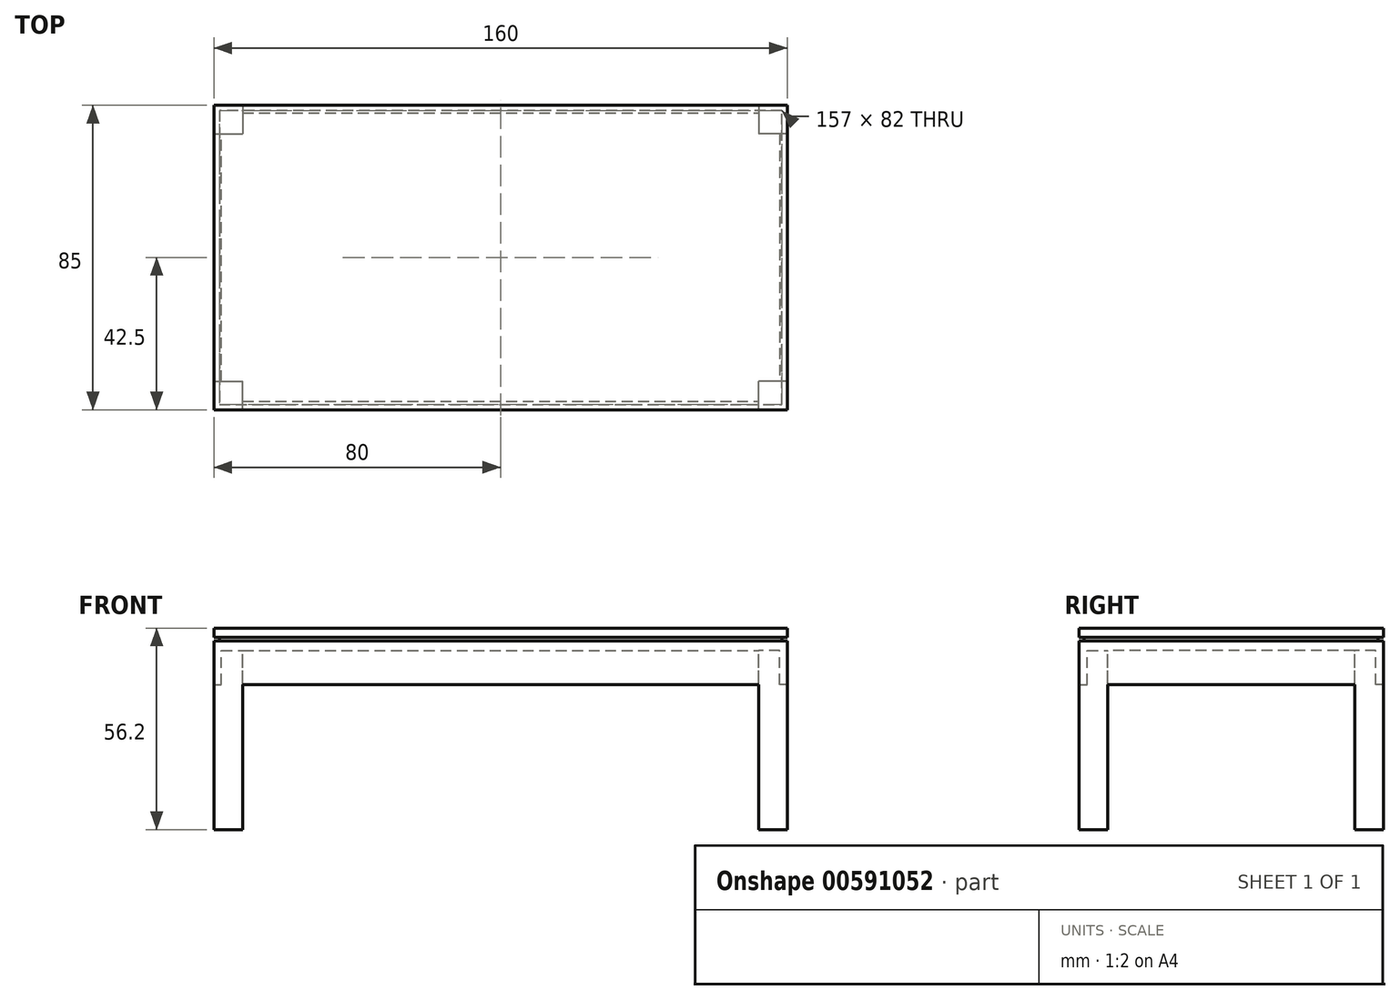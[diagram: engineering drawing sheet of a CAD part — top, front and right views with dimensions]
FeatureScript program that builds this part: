
annotation { "Feature Type Name" : "Feature", "Feature Type Description" : "" }
export const myFeature = defineFeature(function(context is Context, id is Id, definition is map)
    precondition{}
    {
        {
            var Q0;
            Q0=qCreatedBy(makeId("Top.planeOp"),FACE);
            var sketch = newSketch(context, id + "F0", { "sketchPlane" : qUnion([Q0])});
            skLineSegment(sketch, "E0.bottom", {"start": v(0, 0) * mm, "end": v(-160, 0) * mm});
            skLineSegment(sketch, "E0.top", {"start": v(0, 85) * mm, "end": v(-160, 85) * mm});
            skLineSegment(sketch, "E0.left", {"start": v(0, 0) * mm, "end": v(0, 85) * mm});
            skLineSegment(sketch, "E0.right", {"start": v(-160, 0) * mm, "end": v(-160, 85) * mm});
            skSolve(sketch);
        }
        {
            var Q0;
            Q0=makeQuery(id+"F0.imprint","IMPRINT",FACE,{"disambiguationData":[TD([[makeQuery(id+"F0.imprint","IMPRINT",EDGE,{"derivedFrom":sQuery(id+"F0.wireOp",EDGE,"E0.bottom")}),-1.0]])]});
            extrude(context, id + "F1", {"entities" : qUnion([Q0]), "depth" : 2.7 * mm, "offsetDistance" : 25 * mm});
        }
        {
            var Q0;
            Q0=makeQuery(id+"F1.opExtrude","CAP_FACE",FACE,{"disambiguationData":[OSD([sQuery(id+"F0.wireOp",EDGE,"E0.bottom"),sQuery(id+"F0.wireOp",EDGE,"E0.top"),sQuery(id+"F0.wireOp",EDGE,"E0.left"),sQuery(id+"F0.wireOp",EDGE,"E0.right")])],"isStart":false});
            var sketch = newSketch(context, id + "F2", { "sketchPlane" : qUnion([Q0])});
            skLineSegment(sketch, "E1", {"start": v(-80, 85) * mm, "end": v(-80, 83.5) * mm});
            skLineSegment(sketch, "E2", {"start": v(-160, 42.5) * mm, "end": v(-158.5, 42.5) * mm});
            skLineSegment(sketch, "E3", {"start": v(-80, 0) * mm, "end": v(-80, 1.5) * mm});
            skLineSegment(sketch, "E4", {"start": v(0, 42.5) * mm, "end": v(-1.5, 42.5) * mm});
            skLineSegment(sketch, "E5.top", {"start": v(-1.5, 83.5) * mm, "end": v(-80, 83.5) * mm});
            skLineSegment(sketch, "E5.left", {"start": v(-1.5, 42.5) * mm, "end": v(-1.5, 83.5) * mm});
            skLineSegment(sketch, "E6.right", {"start": v(-158.5, 42.5) * mm, "end": v(-158.5, 42.5) * mm});
            skLineSegment(sketch, "E7.bottom", {"start": v(-80, 1.5) * mm, "end": v(-1.5, 1.5) * mm});
            skLineSegment(sketch, "E7.top", {"start": v(-80, 83.5) * mm, "end": v(-1.5, 83.5) * mm});
            skLineSegment(sketch, "E7.right", {"start": v(-1.5, 1.5) * mm, "end": v(-1.5, 83.5) * mm});
            skLineSegment(sketch, "E8.bottom", {"start": v(-80, 83.5) * mm, "end": v(-158.5, 83.5) * mm});
            skLineSegment(sketch, "E8.right", {"start": v(-158.5, 83.5) * mm, "end": v(-158.5, 42.5) * mm});
            skLineSegment(sketch, "E9.top", {"start": v(-158.5, 1.5) * mm, "end": v(-80, 1.5) * mm});
            skLineSegment(sketch, "E9.left", {"start": v(-158.5, 42.5) * mm, "end": v(-158.5, 1.5) * mm});
            skSolve(sketch);
        }
        {
            var Q0;
            Q0 = qSketchRegion(id + "F2", true);
            extrude(context, id + "F3", {"entities" : qUnion([Q0]), "operationType" : NewBodyOperationType.ADD, "depth" : 1 * mm, "offsetDistance" : 25 * mm});
        }
        {
            var Q0;
            Q0=makeQuery(id+"F1.opExtrude","CAP_FACE",FACE,{"disambiguationData":[OSD([sQuery(id+"F0.wireOp",EDGE,"E0.bottom"),sQuery(id+"F0.wireOp",EDGE,"E0.top"),sQuery(id+"F0.wireOp",EDGE,"E0.left"),sQuery(id+"F0.wireOp",EDGE,"E0.right")])],"isStart":true});
            var sketch = newSketch(context, id + "F4", { "sketchPlane" : qUnion([Q0])});
            skLineSegment(sketch, "E10.bottom", {"start": v(-160, 0) * mm, "end": v(-152, 0) * mm});
            skLineSegment(sketch, "E10.top", {"start": v(-160, -8) * mm, "end": v(-152, -8) * mm});
            skLineSegment(sketch, "E10.left", {"start": v(-160, 0) * mm, "end": v(-160, -8) * mm});
            skLineSegment(sketch, "E10.right", {"start": v(-152, 0) * mm, "end": v(-152, -8) * mm});
            skLineSegment(sketch, "E11.bottom", {"start": v(-160, -85) * mm, "end": v(-152, -85) * mm});
            skLineSegment(sketch, "E11.top", {"start": v(-160, -77) * mm, "end": v(-152, -77) * mm});
            skLineSegment(sketch, "E11.left", {"start": v(-160, -85) * mm, "end": v(-160, -77) * mm});
            skLineSegment(sketch, "E11.right", {"start": v(-152, -85) * mm, "end": v(-152, -77) * mm});
            skLineSegment(sketch, "E12.bottom", {"start": v(0, -85) * mm, "end": v(-8, -85) * mm});
            skLineSegment(sketch, "E12.top", {"start": v(0, -77) * mm, "end": v(-8, -77) * mm});
            skLineSegment(sketch, "E12.left", {"start": v(0, -85) * mm, "end": v(0, -77) * mm});
            skLineSegment(sketch, "E12.right", {"start": v(-8, -85) * mm, "end": v(-8, -77) * mm});
            skLineSegment(sketch, "E13.bottom", {"start": v(0, 0) * mm, "end": v(-8, 0) * mm});
            skLineSegment(sketch, "E13.top", {"start": v(0, -8) * mm, "end": v(-8, -8) * mm});
            skLineSegment(sketch, "E13.left", {"start": v(0, 0) * mm, "end": v(0, -8) * mm});
            skLineSegment(sketch, "E13.right", {"start": v(-8, 0) * mm, "end": v(-8, -8) * mm});
            skSolve(sketch);
        }
        {
            var Q0;
            Q0=makeQuery(id+"F4.imprint","IMPRINT",FACE,{"disambiguationData":[TD([[makeQuery(id+"F4.imprint","IMPRINT",EDGE,{"derivedFrom":sQuery(id+"F4.wireOp",EDGE,"E10.bottom")}),1.0]])]});
            extrude(context, id + "F5", {"entities" : qUnion([Q0]), "operationType" : NewBodyOperationType.ADD, "depth" : 50 * mm, "offsetDistance" : 25 * mm});
        }
        {
            var Q0;
            Q0 = qSketchRegion(id + "F4", true);
            extrude(context, id + "F6", {"entities" : qUnion([Q0]), "operationType" : NewBodyOperationType.ADD, "depth" : 50 * mm, "offsetDistance" : 25 * mm});
        }
        {
            var Q0;
            Q0=makeQuery(id+"F3.opExtrude","CAP_FACE",FACE,{"disambiguationData":[OSD([sQuery(id+"F2.wireOp",EDGE,"E7.bottom"),sQuery(id+"F2.wireOp",EDGE,"E7.top"),sQuery(id+"F2.wireOp",EDGE,"E7.right"),sQuery(id+"F2.wireOp",EDGE,"E8.bottom"),sQuery(id+"F2.wireOp",EDGE,"E8.right"),sQuery(id+"F2.wireOp",EDGE,"E9.top"),sQuery(id+"F2.wireOp",EDGE,"E9.left")])],"isStart":false});
            var sketch = newSketch(context, id + "F7", { "sketchPlane" : qUnion([Q0])});
            skLineSegment(sketch, "E14", {"start": v(-158.5, 42.5) * mm, "end": v(-160, 42.5) * mm});
            skLineSegment(sketch, "E15", {"start": v(-80, 1.5) * mm, "end": v(-80, 0) * mm});
            skLineSegment(sketch, "E16", {"start": v(-1.5, 42.5) * mm, "end": v(0, 42.5) * mm});
            skPoint(sketch, "E16.endSnap0", {"position": v(-1.5, 42.5) * mm});
            skLineSegment(sketch, "E17", {"start": v(-80, 83.5) * mm, "end": v(-80, 85) * mm});
            skPoint(sketch, "E17.endSnap0", {"position": v(-80, 83.5) * mm});
            skLineSegment(sketch, "E18.top", {"start": v(-160, 0) * mm, "end": v(-80, 0) * mm});
            skLineSegment(sketch, "E18.left", {"start": v(-160, 42.5) * mm, "end": v(-160, 0) * mm});
            skLineSegment(sketch, "E19.top", {"start": v(0, 0) * mm, "end": v(-80, 0) * mm});
            skLineSegment(sketch, "E19.left", {"start": v(0, 42.5) * mm, "end": v(0, 0) * mm});
            skLineSegment(sketch, "E20.top", {"start": v(0, 85) * mm, "end": v(-80, 85) * mm});
            skLineSegment(sketch, "E20.left", {"start": v(0, 42.5) * mm, "end": v(0, 85) * mm});
            skLineSegment(sketch, "E21.top", {"start": v(-160, 85) * mm, "end": v(-80, 85) * mm});
            skLineSegment(sketch, "E21.left", {"start": v(-160, 42.5) * mm, "end": v(-160, 85) * mm});
            skSolve(sketch);
        }
        {
            var Q0;
            Q0 = qSketchRegion(id + "F7", true);
            extrude(context, id + "F8", {"entities" : qUnion([Q0]), "operationType" : NewBodyOperationType.ADD, "depth" : 2.5 * mm, "offsetDistance" : 25 * mm});
        }
        {
            var Q0;
            Q0=makeQuery(id+"F1.opExtrude","CAP_FACE",FACE,{"disambiguationData":[OSD([sQuery(id+"F0.wireOp",EDGE,"E0.bottom"),sQuery(id+"F0.wireOp",EDGE,"E0.top"),sQuery(id+"F0.wireOp",EDGE,"E0.left"),sQuery(id+"F0.wireOp",EDGE,"E0.right")])],"isStart":true});
            var sketch = newSketch(context, id + "F9", { "sketchPlane" : qUnion([Q0])});
            skLineSegment(sketch, "E22.bottom", {"start": v(-152, 0) * mm, "end": v(-8, 0) * mm});
            skLineSegment(sketch, "E22.top", {"start": v(-152, -2.39) * mm, "end": v(-8, -2.39) * mm});
            skLineSegment(sketch, "E22.left", {"start": v(-152, 0) * mm, "end": v(-152, -2.39) * mm});
            skLineSegment(sketch, "E22.right", {"start": v(-8, 0) * mm, "end": v(-8, -2.39) * mm});
            skLineSegment(sketch, "E23.bottom", {"start": v(-160, -8) * mm, "end": v(-157.9, -8) * mm});
            skLineSegment(sketch, "E23.top", {"start": v(-160, -77) * mm, "end": v(-157.9, -77) * mm});
            skLineSegment(sketch, "E23.left", {"start": v(-160, -8) * mm, "end": v(-160, -77) * mm});
            skLineSegment(sketch, "E23.right", {"start": v(-157.9, -8) * mm, "end": v(-157.9, -77) * mm});
            skLineSegment(sketch, "E24.bottom", {"start": v(0, -77) * mm, "end": v(-2.1, -77) * mm});
            skLineSegment(sketch, "E24.top", {"start": v(0, -8) * mm, "end": v(-2.1, -8) * mm});
            skLineSegment(sketch, "E24.left", {"start": v(0, -77) * mm, "end": v(0, -8) * mm});
            skLineSegment(sketch, "E24.right", {"start": v(-2.1, -77) * mm, "end": v(-2.1, -8) * mm});
            skLineSegment(sketch, "E25.bottom", {"start": v(-152, -85) * mm, "end": v(-8, -85) * mm});
            skLineSegment(sketch, "E25.top", {"start": v(-152, -82.9) * mm, "end": v(-8, -82.9) * mm});
            skLineSegment(sketch, "E25.left", {"start": v(-152, -85) * mm, "end": v(-152, -82.9) * mm});
            skLineSegment(sketch, "E25.right", {"start": v(-8, -85) * mm, "end": v(-8, -82.9) * mm});
            skSolve(sketch);
        }
        {
            var Q0;
            Q0 = qSketchRegion(id + "F9", true);
            extrude(context, id + "F10", {"entities" : qUnion([Q0]), "operationType" : NewBodyOperationType.ADD, "depth" : 9.5 * mm, "offsetDistance" : 25 * mm});
        }
    });
